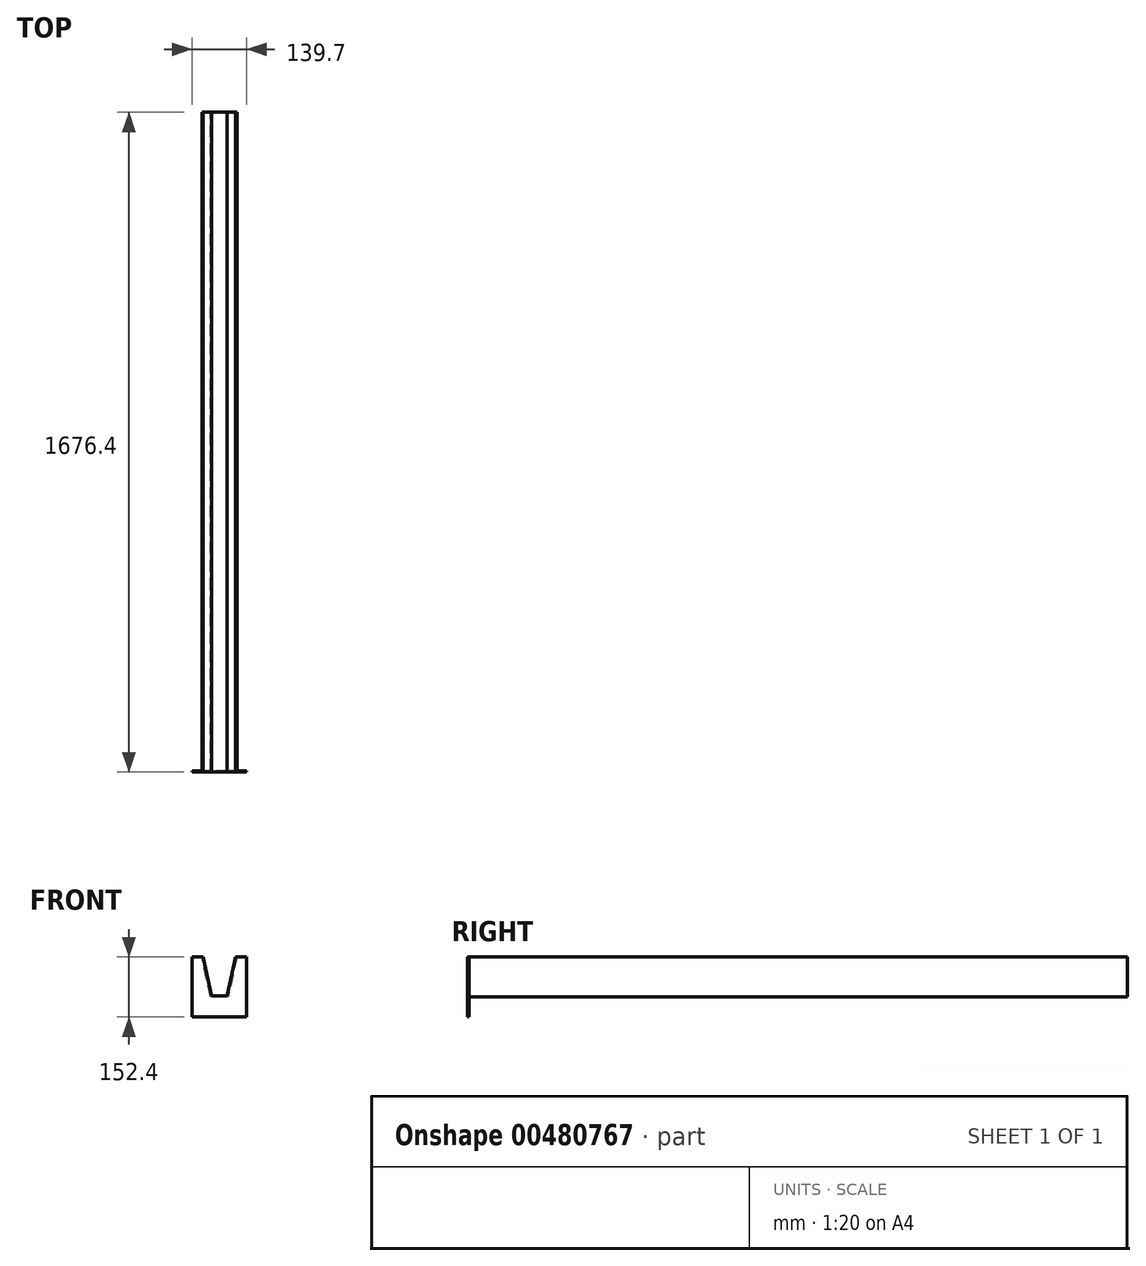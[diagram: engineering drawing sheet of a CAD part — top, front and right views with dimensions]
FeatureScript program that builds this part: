
annotation { "Feature Type Name" : "Feature", "Feature Type Description" : "" }
export const myFeature = defineFeature(function(context is Context, id is Id, definition is map)
    precondition{}
    {
        {
            var Q0;
            Q0=qCreatedBy(makeId("Front.planeOp"),FACE);
            var sketch = newSketch(context, id + "F0", { "sketchPlane" : qUnion([Q0])});
            skLineSegment(sketch, "E0", {"start": v(0, 0) * mm, "end": v(-22.23, 0) * mm});
            skLineSegment(sketch, "E1", {"start": v(-22.22, 0) * mm, "end": v(-44.45, 101.6) * mm});
            skLineSegment(sketch, "E2", {"start": v(-44.45, 101.6) * mm, "end": v(44.45, 101.6) * mm});
            skLineSegment(sketch, "E3", {"start": v(44.45, 101.6) * mm, "end": v(22.23, 0) * mm});
            skLineSegment(sketch, "E4", {"start": v(22.23, 0) * mm, "end": v(0, 0) * mm});
            skSolve(sketch);
        }
        {
            var Q0;
            Q0 = qSketchRegion(id + "F0", true);
            extrude(context, id + "F1", {"entities" : qUnion([Q0]), "depth" : 1676.4 * mm});
        }
        {
            var Q0;
            Q0=makeQuery(id+"F1.opExtrude","SWEPT_FACE",FACE,{"disambiguationData":[OSD([sQuery(id+"F0.wireOp",EDGE,"E2")])]});
            shell(context, id + "F2", {"entities" : qUnion([Q0]), "thickness" : 3.17 * mm});
        }
        {
            var Q0;
            {var subQ0=sQuery(id+"F0.wireOp",EDGE,"E4");var subQ1=sQuery(id+"F0.wireOp",EDGE,"E3");var subQ2=sQuery(id+"F0.wireOp",EDGE,"E2");var subQ3=sQuery(id+"F0.wireOp",EDGE,"E1");var subQ4=sQuery(id+"F0.wireOp",EDGE,"E0");Q0=makeQuery(id+"F2.opShell","OFFSET_FACE",FACE,{"disambiguationData":[OSD([subQ4,subQ3,subQ2,subQ1,subQ0]),TDD([makeQuery(id+"F1.opExtrude","CAP_FACE",FACE,{"disambiguationData":[OSD([subQ4,subQ3,subQ2,subQ1,subQ0])],"isStart":false})])]});}
            extrude(context, id + "F3", {"entities" : qUnion([Q0]), "operationType" : NewBodyOperationType.REMOVE, "oppositeDirection" : true, "depth" : 25.4 * mm});
        }
        {
            var Q0;
            {var subQ0=sQuery(id+"F0.wireOp",EDGE,"E4");var subQ1=sQuery(id+"F0.wireOp",EDGE,"E3");var subQ2=sQuery(id+"F0.wireOp",EDGE,"E2");var subQ3=sQuery(id+"F0.wireOp",EDGE,"E1");var subQ4=sQuery(id+"F0.wireOp",EDGE,"E0");Q0=makeQuery(id+"F2.opShell","OFFSET_FACE",FACE,{"disambiguationData":[OSD([subQ4,subQ3,subQ2,subQ1,subQ0]),TDD([makeQuery(id+"F1.opExtrude","CAP_FACE",FACE,{"disambiguationData":[OSD([subQ4,subQ3,subQ2,subQ1,subQ0])],"isStart":true})])]});}
            extrude(context, id + "F4", {"entities" : qUnion([Q0]), "operationType" : NewBodyOperationType.REMOVE, "oppositeDirection" : true, "depth" : 25.4 * mm});
        }
        {
            var Q0;
            Q0=makeQuery(id+"F1.opExtrude","CAP_FACE",FACE,{"disambiguationData":[OSD([sQuery(id+"F0.wireOp",EDGE,"E0"),sQuery(id+"F0.wireOp",EDGE,"E1"),sQuery(id+"F0.wireOp",EDGE,"E2"),sQuery(id+"F0.wireOp",EDGE,"E3"),sQuery(id+"F0.wireOp",EDGE,"E4")])],"isStart":false});
            var sketch = newSketch(context, id + "F5", { "sketchPlane" : qUnion([Q0])});
            skLineSegment(sketch, "E5", {"start": v(44.45, 101.6) * mm, "end": v(69.85, 101.6) * mm});
            skLineSegment(sketch, "E6", {"start": v(69.85, 101.6) * mm, "end": v(69.85, -50.8) * mm});
            skLineSegment(sketch, "E7", {"start": v(69.85, -50.8) * mm, "end": v(-69.85, -50.8) * mm});
            skLineSegment(sketch, "E8", {"start": v(-69.85, -50.8) * mm, "end": v(-69.85, 101.6) * mm});
            skLineSegment(sketch, "E9", {"start": v(-69.85, 101.6) * mm, "end": v(-44.45, 101.6) * mm});
            skLineSegment(sketch, "E10", {"start": v(-44.45, 101.6) * mm, "end": v(-22.23, 0) * mm});
            skLineSegment(sketch, "E11", {"start": v(-22.23, 0) * mm, "end": v(22.23, 0) * mm});
            skLineSegment(sketch, "E12", {"start": v(22.23, 0) * mm, "end": v(44.45, 101.6) * mm});
            skSolve(sketch);
        }
        {
            var Q0;
            Q0=makeQuery(id+"F5.imprint","IMPRINT",FACE,{"disambiguationData":[TD([[makeQuery(id+"F5.imprint","IMPRINT",EDGE,{"derivedFrom":sQuery(id+"F5.wireOp",EDGE,"E5")}),-1.0]])]});
            extrude(context, id + "F6", {"entities" : qUnion([Q0]), "operationType" : NewBodyOperationType.ADD, "oppositeDirection" : true, "depth" : 3.17 * mm});
        }
    });
